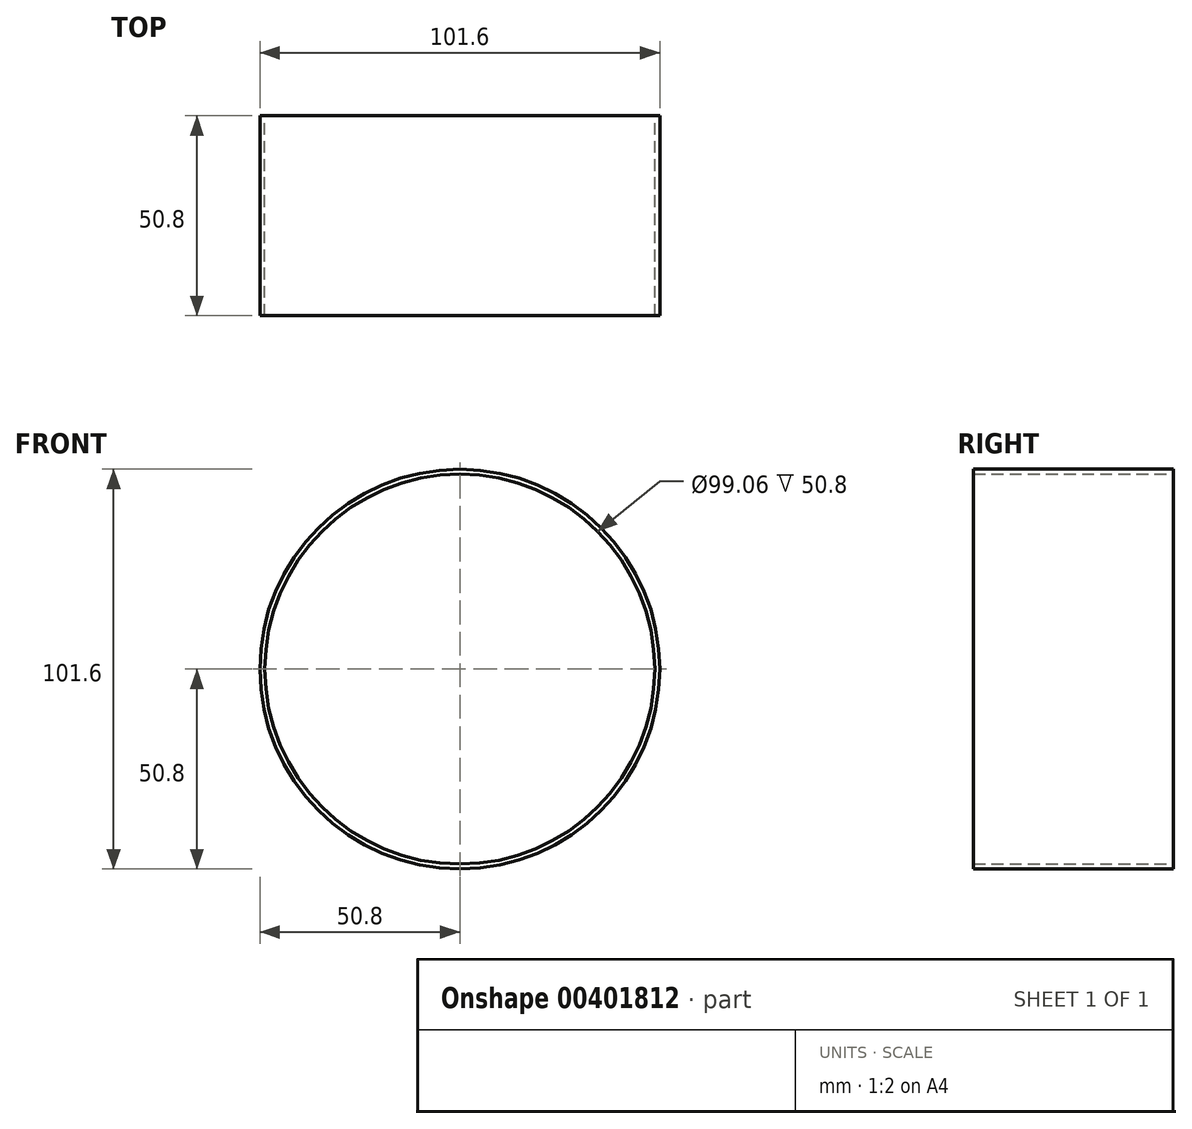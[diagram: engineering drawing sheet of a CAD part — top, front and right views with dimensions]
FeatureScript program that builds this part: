
annotation { "Feature Type Name" : "Feature", "Feature Type Description" : "" }
export const myFeature = defineFeature(function(context is Context, id is Id, definition is map)
    precondition{}
    {
        {
            var Q0;
            Q0=qCreatedBy(makeId("Front.planeOp"),FACE);
            var sketch = newSketch(context, id + "F0", { "sketchPlane" : qUnion([Q0])});
            skCircle(sketch, "E0", {"center": v(0, 0) * mm, "radius": 50.8 * mm});
            skCircle(sketch, "E1", {"center": v(0, 0) * mm, "radius": 49.53 * mm});
            skSolve(sketch);
        }
        {
            var Q0;
            Q0=makeQuery(id+"F0.imprint","IMPRINT",FACE,{"disambiguationData":[TD([[makeQuery(id+"F0.imprint","IMPRINT",EDGE,{"derivedFrom":sQuery(id+"F0.wireOp",EDGE,"E0")}),1.0]])]});
            extrude(context, id + "F1", {"entities" : qUnion([Q0]), "depth" : 50.8 * mm});
        }
    });
